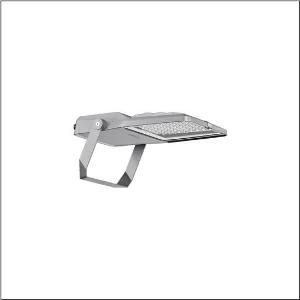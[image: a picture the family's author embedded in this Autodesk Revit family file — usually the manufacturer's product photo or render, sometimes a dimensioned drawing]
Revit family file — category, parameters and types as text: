
# Revit family: floodlight_fl_21_iq_mini___pl61_5xa7772d4c1a_f35a
name_source: partatom
category: Lighting Fixtures
units: mm (PartAtom-declared; Revit-internal decimal feet)

## family parameters
Cut with Voids When Loaded = No
Host = Face
Light Source = No
Part Type = Normal
Room Calculation Point = No
Round Connector Dimension = Use Diameter
Shared = No

## types (1)
- --- (1 x LED, 18260 lm, 143 W, 4000K)
    Apparent Load = 143 VA
    CIE Flux Codes = 33 65 98 100 100
    Color Rendering = 70
    Color Temperature = 4000K
    Default Elevation = 1800 mm
    Description = Floodlight FL 21 iQ mini, floodlight, primary light control with lens, of PMMA, primary optical cover: protective disc, of toughened safety glass, transparent, light distribution: PL61, light emission: direct distribution, installation type: surface-mounted, LED, High Power LED, rated luminous flux: 18.260lm, luminous efficacy: 128lm/W, light colour: 740, colour temperature: 4000K, control: Street-Remote, Auto-Match, Temp-Guard, Night-Set, Smart-Wire, Desk-Remote (wireless, voltage-free reading and setting of iQ features in the workshop via application-optimized NFC function/RFID function), optimised constant luminous flux control (CLO 2.0), with terminal, 6-pole, mains connection: 220..240V, AC, 50/60Hz, start of lifetime: 143W, end of service life: 152W, reduction: 61W, luminaire housing, of diecast aluminium, powder-coated, Siteco® metallic grey (DB 702S), corrosivity category C5 mid according to DIN EN ISO 12944, sealing non-destructively replaceable, mounting bracket, of steel, galvanised, powder-coated, Siteco® metallic grey (DB 702S), protection rating (complete): IP66, insulation class (complete): insulation class II (safety insulation), certification: CE, ENEC, VDE, protection symbol: D, impact resistance: IK08, permissible operating ambient temperature: -40..+40°C, permissible operating ambient temperature for outdoor applications: -40..+50°C, standard: DIN EN 12944, LABS conformity tested according to VDMA 24364:2018-05, packaging unit: 1 piece

Light Distribution: PL61
    Height = 70 mm
    Lamp = 1 x LED
    Lamp Light Flux = 18260 lm
    Lamp Power = 143 W
    Lamp count = 1
    Length = 485 mm
    Luminous efficacy = 128 lm/W
    Manufacturer = Siteco
    ModVariant = No
    Model = 5XA7772D4C1A
    Number of Poles = 1
    OnlyDefault = Yes
    Power Factor = 1
    Product Name = Floodlight FL 21 iQ mini | PL61
    Product group = floodlight | pylon annexe
    ProductGroupID = 6200
    Protection Class = Protection class II
    Protection Degree = IP 66
    RLX_Detail_Level = 1
    RLX_Emergency_Light_Flux = 0 lm
    RLX_Emergency_Type = 0
    RLX_Emergency_Type_DB = No
    RlxData = <blob elided: 96461 chars, md5=7c32df63>
    Socket = socket
    Standby Power = 0 W
    System Light Flux = 18260 lm
    System Power = 143 W
    Type Comments = factory setting: luminous flux: 100 % | dim-lin: 254 | 730 mA
    Type Image = l_1006845.jpg
    URL = http://relux.com
    VarID = @adj_123303
    Voltage = 0 V
    Weight = 0.00 kg
    Width = 337 mm

## geometry (parser evidence)
native form markers: Blend x4, Sweep x11
no freeform markers — native parametric forms only
